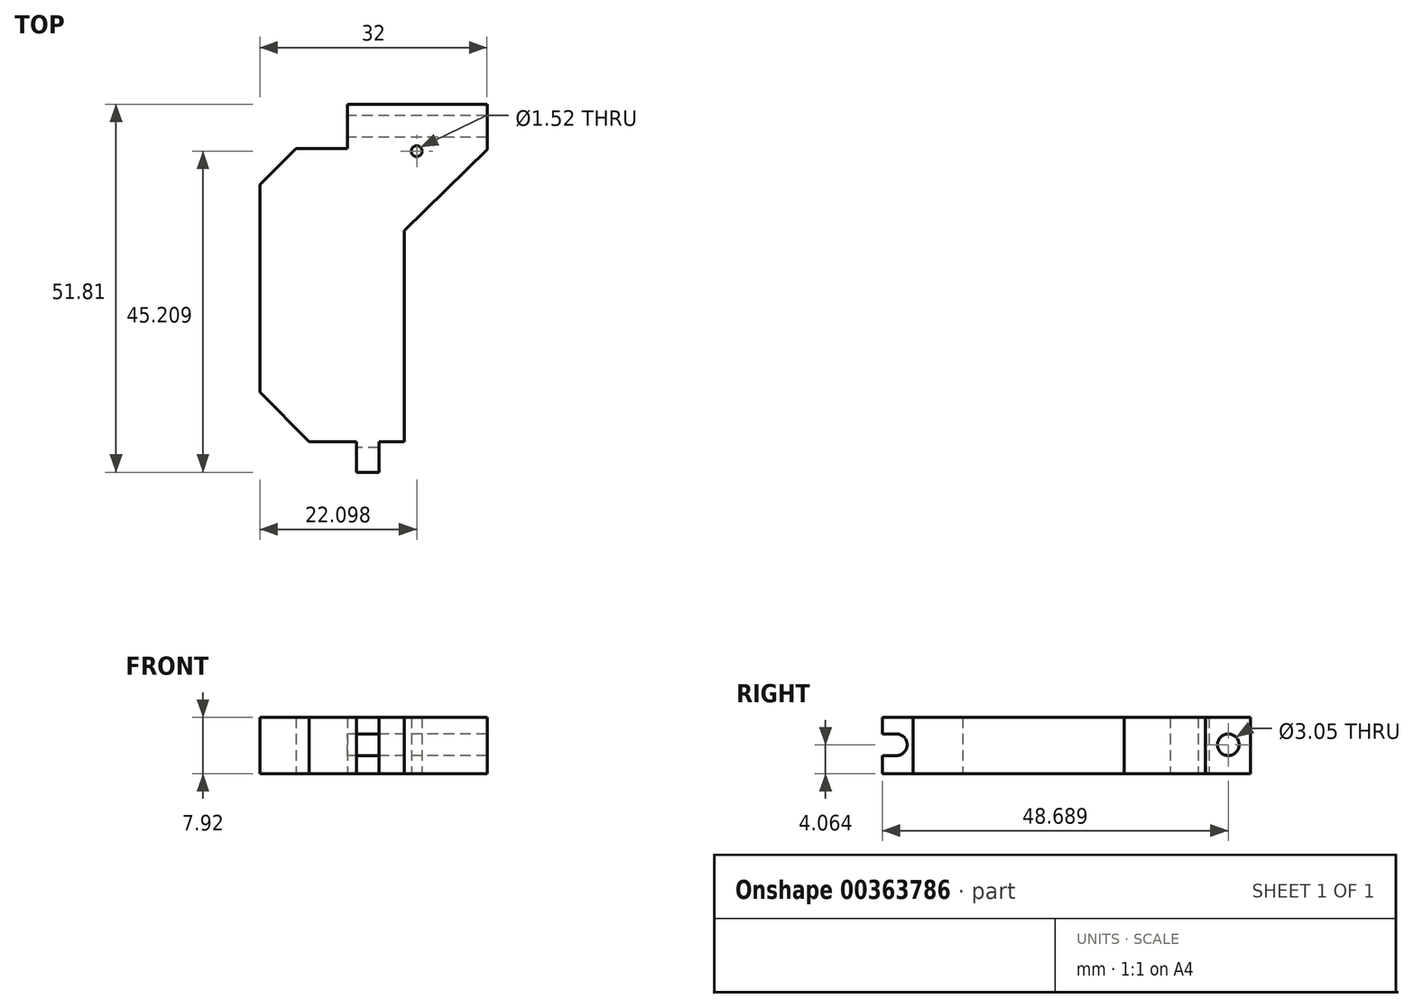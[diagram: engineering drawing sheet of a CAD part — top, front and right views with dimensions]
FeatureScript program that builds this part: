
annotation { "Feature Type Name" : "Feature", "Feature Type Description" : "" }
export const myFeature = defineFeature(function(context is Context, id is Id, definition is map)
    precondition{}
    {
        {
            var Q0;
            Q0=qCreatedBy(makeId("Top.planeOp"),FACE);
            var sketch = newSketch(context, id + "F0", { "sketchPlane" : qUnion([Q0])});
            skLineSegment(sketch, "E0.bottom", {"start": v(32, 40.51) * mm, "end": v(12.32, 40.51) * mm});
            skLineSegment(sketch, "E0.left", {"start": v(32, 40.51) * mm, "end": v(32, 34.16) * mm});
            skLineSegment(sketch, "E0.right", {"start": v(12.32, 40.51) * mm, "end": v(12.32, 34.3) * mm});
            skCircle(sketch, "E1", {"center": v(22.1, 33.9) * mm, "radius": 0.76 * mm});
            skLineSegment(sketch, "E2", {"start": v(32, 34.16) * mm, "end": v(20.32, 22.73) * mm});
            skLineSegment(sketch, "E3", {"start": v(12.32, 34.3) * mm, "end": v(5.08, 34.3) * mm});
            skLineSegment(sketch, "E4", {"start": v(5.08, 34.3) * mm, "end": v(0, 29.21) * mm});
            skLineSegment(sketch, "E5", {"start": v(0, 29.21) * mm, "end": v(0, 0) * mm});
            skLineSegment(sketch, "E6", {"start": v(0, 0) * mm, "end": v(6.99, -6.99) * mm});
            skLineSegment(sketch, "E7", {"start": v(6.99, -6.99) * mm, "end": v(13.59, -6.99) * mm});
            skLineSegment(sketch, "E8", {"start": v(13.59, -6.99) * mm, "end": v(13.59, -11.3) * mm});
            skLineSegment(sketch, "E9", {"start": v(13.59, -11.3) * mm, "end": v(16.76, -11.3) * mm});
            skLineSegment(sketch, "E10", {"start": v(16.76, -11.3) * mm, "end": v(16.76, -6.99) * mm});
            skLineSegment(sketch, "E11", {"start": v(16.76, -6.99) * mm, "end": v(20.32, -6.99) * mm});
            skLineSegment(sketch, "E12", {"start": v(20.32, -6.99) * mm, "end": v(20.32, 22.73) * mm});
            skSolve(sketch);
        }
        {
            var Q0;
            Q0=makeQuery(id+"F0.imprint","IMPRINT",FACE,{"disambiguationData":[TD([[makeQuery(id+"F0.imprint","IMPRINT",EDGE,{"derivedFrom":sQuery(id+"F0.wireOp",EDGE,"E0.bottom")}),1.0]])]});
            extrude(context, id + "F1", {"entities" : qUnion([Q0]), "depth" : 7.92 * mm});
        }
        {
            var Q0;
            Q0=qCreatedBy(makeId("Right.planeOp"),FACE);
            var sketch = newSketch(context, id + "F2", { "sketchPlane" : qUnion([Q0])});
            skCircle(sketch, "E13", {"center": v(37.39, 4.06) * mm, "radius": 1.52 * mm});
            skLineSegment(sketch, "E14.0.0", {"start": v(34.16, 0) * mm, "end": v(40.51, 0) * mm, "construction": true});
            skLineSegment(sketch, "E14.0.1", {"start": v(40.51, 0) * mm, "end": v(40.51, 7.92) * mm, "construction": true});
            skLineSegment(sketch, "E14.0.2", {"start": v(40.51, 7.92) * mm, "end": v(34.16, 7.92) * mm, "construction": true});
            skLineSegment(sketch, "E14.0.3", {"start": v(34.16, 7.92) * mm, "end": v(34.16, 0) * mm, "construction": true});
            skLineSegment(sketch, "E15.0.0", {"start": v(-11.3, 0) * mm, "end": v(-6.99, 0) * mm, "construction": true});
            skLineSegment(sketch, "E15.0.1", {"start": v(-6.99, 0) * mm, "end": v(-6.99, 7.92) * mm, "construction": true});
            skLineSegment(sketch, "E15.0.2", {"start": v(-6.99, 7.92) * mm, "end": v(-11.3, 7.92) * mm, "construction": true});
            skLineSegment(sketch, "E15.0.3", {"start": v(-11.3, 7.92) * mm, "end": v(-11.3, 0) * mm, "construction": true});
            skArc(sketch, "E16", {"start": v(-9.35, 2.54) * mm, "mid": v(-7.82, 4.06) * mm, "end": v(-9.35, 5.59) * mm});
            skLineSegment(sketch, "E17", {"start": v(-9.35, 5.59) * mm, "end": v(-11.3, 5.59) * mm});
            skLineSegment(sketch, "E18", {"start": v(-9.35, 2.54) * mm, "end": v(-11.3, 2.54) * mm});
            skLineSegment(sketch, "E19", {"start": v(-11.3, 2.54) * mm, "end": v(-11.3, 5.59) * mm});
            skSolve(sketch);
        }
        {
            var Q0;
            Q0 = qSketchRegion(id + "F2", true);
            extrude(context, id + "F3", {"entities" : qUnion([Q0]), "operationType" : NewBodyOperationType.REMOVE, "endBound" : BoundingType.THROUGH_ALL, "depth" : 25.4 * mm});
        }
    });
